# Revit family: Robusta 300
name_source: partatom
category: Mechanical Equipment
revit_build: Autodesk Revit 2018 (Build: 20170223_1515(x64)
units: mm (PartAtom-declared; Revit-internal decimal feet)

## family parameters
Always vertical = Yes
Cut with Voids When Loaded = No
Part Type = Normal
Room Calculation Point = No
Round Connector Dimension = Use Radius
Shared = No
Work Plane-Based = No

## types (1)
- Robusta WTS 300
    Cable = Neoprene
    Cable Length (m) = 10
    Cable Type (H07RN-F) = 3G1.0
    Capacity(m3/hr) = 13.8 m³
    Description = Plug-in, submersible pump, for the removal of wastewater
containing solids up to 10 mm.
pumping clear water, wastewater and sewage from buildings
and sites in domestic and commercial areas.
    Discharge DN 32 = 16 mm  [stored 0.0524934 ft]
    Head(m) = 9 mm  [stored 0.0295276 ft]
    Impeller = PA
    Manufacturer = Sulzer
    Model = Light Drainage Pump Type ABS Robusta 300
    Motor Housing = Stainless steel 1.4301 (AISI 304)
    Motor Power (kW) = P1=0.50
    Motor Shaft = Stainless steel 1.4057 (AISI 431)
    Product Specification Link = https://www.sulzer.com
    Pump Casing = PP
    Pump Casing (Black Colour) = PP (Black)
    Rated Current (A) = 2.2
    Rated Voltage (V) = 220-240 1~
    Seals = NBR

note: [stored X ft] marks values corroborated as IEEE doubles in the binary element streams (Revit-internal decimal feet)

## geometry (parser evidence)
native form markers: Sweep x3
no freeform markers — native parametric forms only
